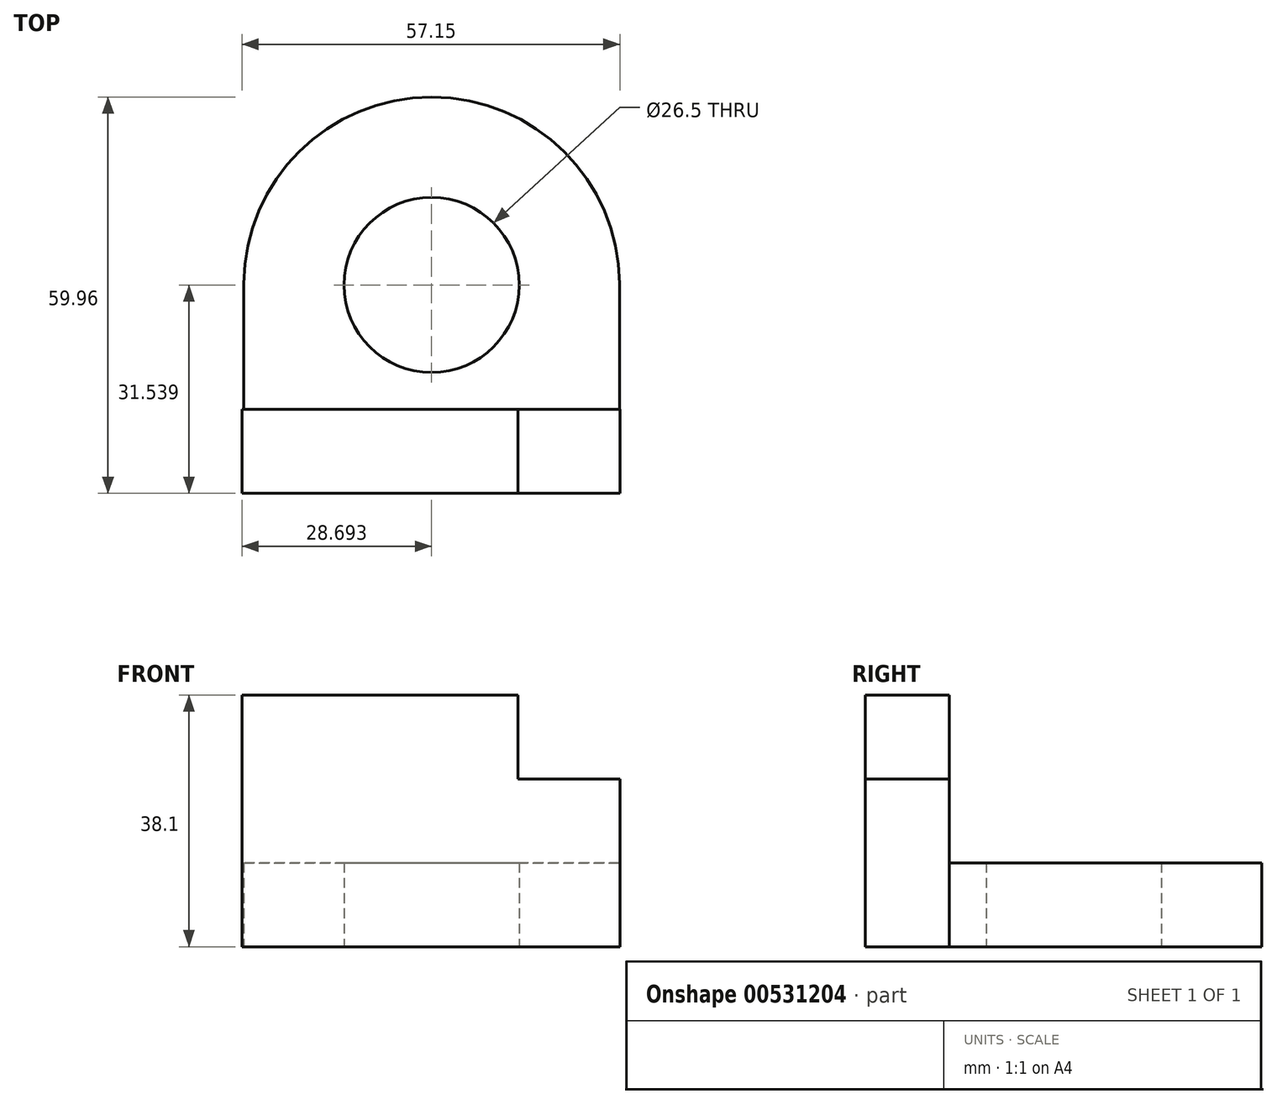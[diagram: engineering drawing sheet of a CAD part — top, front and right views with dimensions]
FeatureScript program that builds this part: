
annotation { "Feature Type Name" : "Feature", "Feature Type Description" : "" }
export const myFeature = defineFeature(function(context is Context, id is Id, definition is map)
    precondition{}
    {
        {
            var Q0;
            Q0=qCreatedBy(makeId("Front.planeOp"),FACE);
            var sketch = newSketch(context, id + "F0", { "sketchPlane" : qUnion([Q0])});
            skLineSegment(sketch, "E0.bottom", {"start": v(-27.37, 0) * mm, "end": v(14.38, 0) * mm});
            skLineSegment(sketch, "E0.top", {"start": v(-27.37, 38.1) * mm, "end": v(14.38, 38.1) * mm});
            skLineSegment(sketch, "E0.left", {"start": v(-27.37, 0) * mm, "end": v(-27.37, 38.1) * mm});
            skLineSegment(sketch, "E0.right", {"start": v(14.38, 0) * mm, "end": v(14.38, 38.1) * mm});
            skLineSegment(sketch, "E1.bottom", {"start": v(14.38, 25.4) * mm, "end": v(29.78, 25.4) * mm});
            skLineSegment(sketch, "E1.top", {"start": v(14.38, 0) * mm, "end": v(29.78, 0) * mm});
            skLineSegment(sketch, "E1.left", {"start": v(14.38, 25.4) * mm, "end": v(14.38, 0) * mm});
            skLineSegment(sketch, "E1.right", {"start": v(29.78, 25.4) * mm, "end": v(29.78, 0) * mm});
            skSolve(sketch);
        }
        {
            var Q0;
            Q0=makeQuery(id+"F0.imprint","IMPRINT",FACE,{"disambiguationData":[TD([[makeQuery(id+"F0.imprint","IMPRINT",EDGE,{"derivedFrom":sQuery(id+"F0.wireOp",EDGE,"E0.bottom")}),1.0]])]});
            var Q1;
            Q1=makeQuery(id+"F0.imprint","IMPRINT",FACE,{"disambiguationData":[TD([[makeQuery(id+"F0.imprint","IMPRINT",EDGE,{"derivedFrom":sQuery(id+"F0.wireOp",EDGE,"E1.bottom")}),-1.0]])]});
            extrude(context, id + "F1", {"entities" : qUnion([Q0, Q1]), "depth" : 12.7 * mm, "offsetDistance" : 25.4 * mm});
        }
        {
            var Q0;
            Q0=qCreatedBy(makeId("Top.planeOp"),FACE);
            var sketch = newSketch(context, id + "F2", { "sketchPlane" : qUnion([Q0])});
            skLineSegment(sketch, "E2.bottom", {"start": v(-27.1, 0) * mm, "end": v(29.74, 0) * mm});
            skLineSegment(sketch, "E2.top", {"start": v(-27.1, 0) * mm, "end": v(29.74, 0) * mm});
            skLineSegment(sketch, "E2.left", {"start": v(-27.1, 0) * mm, "end": v(-27.1, 0) * mm});
            skLineSegment(sketch, "E2.right", {"start": v(29.74, 0) * mm, "end": v(29.74, 0) * mm});
            skLineSegment(sketch, "E3.top", {"start": v(-27.1, 19.09) * mm, "end": v(29.74, 19.09) * mm});
            skLineSegment(sketch, "E3.left", {"start": v(-27.1, 0) * mm, "end": v(-27.1, 19.09) * mm});
            skLineSegment(sketch, "E3.right", {"start": v(29.74, 0) * mm, "end": v(29.74, 19.09) * mm});
            skCircle(sketch, "E4", {"center": v(1.32, 18.84) * mm, "radius": 28.42 * mm});
            skPoint(sketch, "E4.third.point", {"position": v(3.22, -9.52) * mm});
            skCircle(sketch, "E5", {"center": v(1.32, 18.84) * mm, "radius": 13.25 * mm});
            skSolve(sketch);
        }
        {
            var Q0;
            {var subQ0=sQuery(id+"F2.wireOp",EDGE,"E3.top");Q0=makeQuery(id+"F2.imprint","IMPRINT",FACE,{"disambiguationData":[TD([[makeQuery(id+"F2.imprint","IMPRINT",EDGE,{"derivedFrom":subQ0}),1.0]])]});}
            var Q1;
            {var subQ2=sQuery(id+"F2.wireOp",EDGE,"E3.top");Q1=makeQuery(id+"F2.imprint","IMPRINT",FACE,{"disambiguationData":[TD([[makeQuery(id+"F2.imprint","IMPRINT",EDGE,{"derivedFrom":subQ2}),-1.0]])]});}
            var Q2;
            {var subQ0=sQuery(id+"F2.wireOp",EDGE,"E3.right");var subQ1=sQuery(id+"F2.wireOp",EDGE,"E2.bottom");var subQ2=makeQuery(id+"F2.imprint","INTERSECT",VERTEX,{"derivedFrom":[subQ1,subQ0]});Q2=makeQuery(id+"F2.imprint","IMPRINT",FACE,{"disambiguationData":[TD([[makeQuery(id+"F2.imprint","IMPRINT",EDGE,{"disambiguationData":[TD([[subQ2,1.0]])],"derivedFrom":subQ1}),1.0]])]});}
            var Q3;
            {var subQ0=sQuery(id+"F2.wireOp",EDGE,"E3.left");var subQ1=sQuery(id+"F2.wireOp",EDGE,"E2.bottom");var subQ2=makeQuery(id+"F2.imprint","INTERSECT",VERTEX,{"derivedFrom":[subQ1,subQ0]});Q3=makeQuery(id+"F2.imprint","IMPRINT",FACE,{"disambiguationData":[TD([[makeQuery(id+"F2.imprint","IMPRINT",EDGE,{"disambiguationData":[TD([[subQ2,-1.0]])],"derivedFrom":subQ1}),1.0]])]});}
            extrude(context, id + "F3", {"entities" : qUnion([Q0, Q1, Q2, Q3]), "operationType" : NewBodyOperationType.ADD, "depth" : 12.7 * mm, "offsetDistance" : 25.4 * mm});
        }
    });
